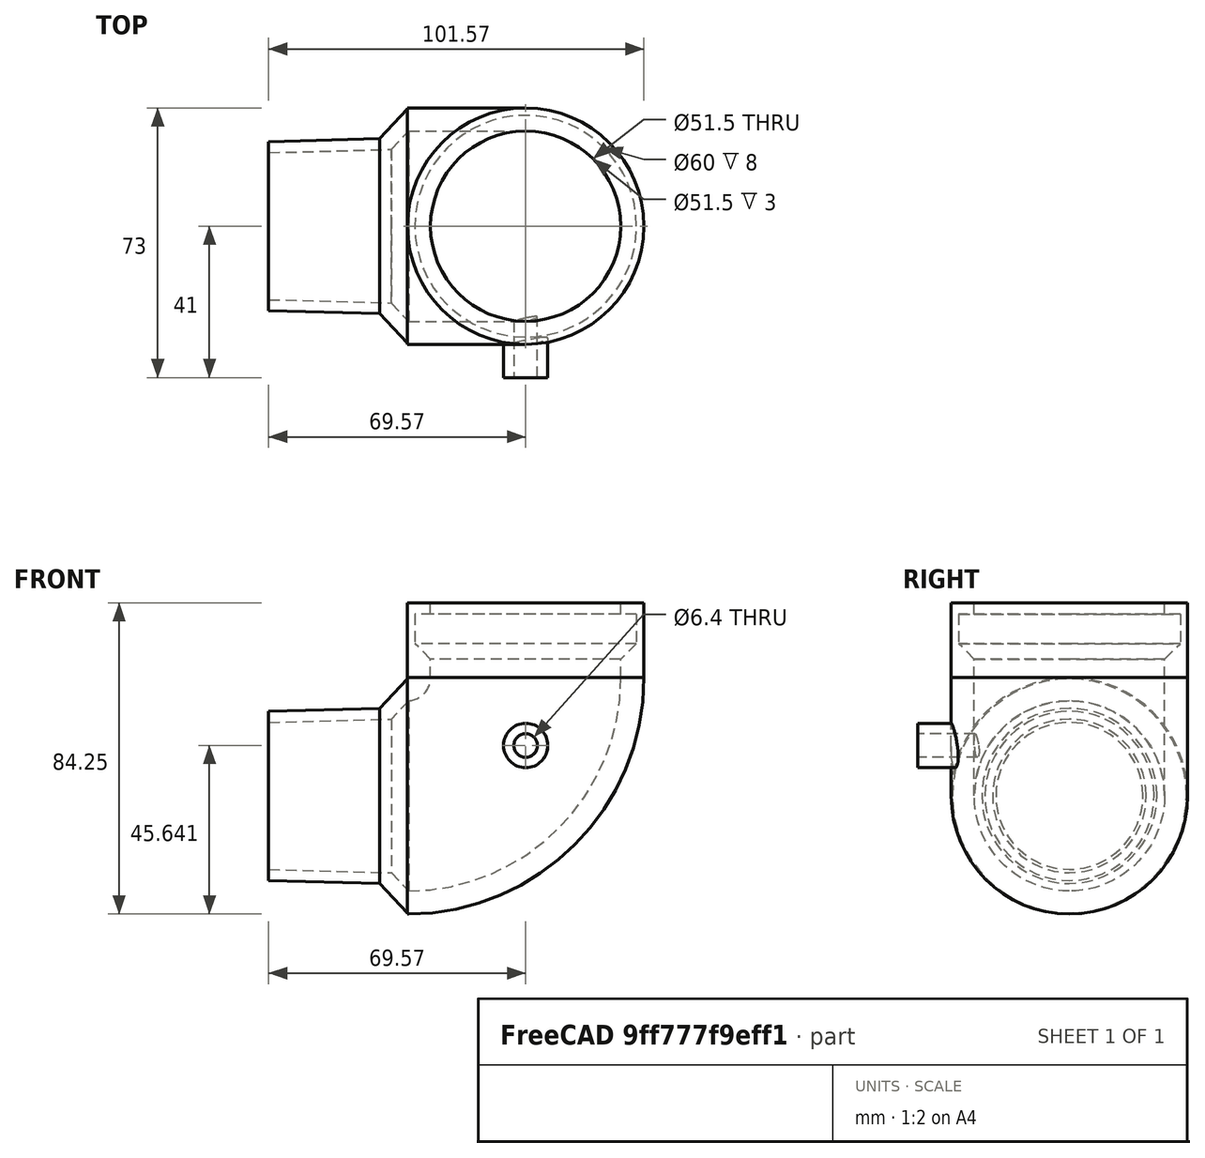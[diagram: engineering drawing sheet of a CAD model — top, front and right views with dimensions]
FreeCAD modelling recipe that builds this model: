
FCSTD DOCUMENT  (FreeCAD 1.1R39747 (Git))
Label: горло (7)
License: All rights reserved
LicenseURL: https://en.wikipedia.org/wiki/All_rights_reserved
objects: Sketcher::SketchObject×5, PartDesign::Revolution×2, App::Point×1, PartDesign::AdditivePipe×1, Part::DatumLine×1, PartDesign::Pad×1, PartDesign::Pocket×1, PartDesign::Body×1
note: 26 computed .brp shape members not serialized (recipe doc carries the construction recipe); baked Part::Feature solids carry a one-line shape summary decoded from their .brp

FEATURE [App::Point] Origin001
  Role = Origin
FEATURE [Sketcher::SketchObject] Sketch
  ArcFitTolerance = 1e-06
  AttachmentSupport = -> [XZ_Plane]
  ExternalTypes = [0]
  FullyConstrained = true
  MakeInternals = false
  MapMode = 5
  Placement = pos=(0,0,0) rot=(1,0,0;1.5708rad)
  expr: Constraints[16] = 63 / 2 - 1.8 + 0.3
  expr: Constraints[17] = 50 / 2 + 0.75
  sketch-geometry (8):
    g0: LineSegment StartX=25.75 StartY=0 StartZ=0 EndX=25.75 EndY=5 EndZ=0
    g1: LineSegment StartX=30 StartY=17.25 StartZ=0 EndX=30 EndY=9.25 EndZ=0
    g2: LineSegment StartX=30 StartY=9.25 StartZ=0 EndX=25.75 EndY=5 EndZ=0
    g3: LineSegment StartX=30 StartY=17.25 StartZ=0 EndX=25.75 EndY=17.25 EndZ=0
    g4: LineSegment StartX=25.75 StartY=17.25 StartZ=0 EndX=25.75 EndY=20.25 EndZ=0
    g5: LineSegment StartX=25.75 StartY=20.25 StartZ=0 EndX=32 EndY=20.25 EndZ=0
    g6: LineSegment StartX=32 StartY=20.25 StartZ=0 EndX=32 EndY=0 EndZ=0
    g7: LineSegment StartX=25.75 StartY=0 StartZ=0 EndX=32 EndY=0 EndZ=0
  constraints (25):
    c: Vertical(g0)
    c: Vertical(g1)
    c: Coincident(g2,g0)
    c: Coincident(g1,g2)
    c: Distance(g1,g1) = 8
    c: Coincident(g3,g1)
    c: Horizontal(g3)
    c: Coincident(g4,g3)
    c: Vertical(g4)
    c: Coincident(g5,g4)
    c: Horizontal(g5)
    c: Coincident(g6,g5)
    c: Vertical(g6)
    c: Distance(g3,g4) = 3  'L1'
    c: DistanceX(g1,g6) = 2
    c: Angle(g0,g2) = 2.35619
    c: DistanceX(g-1,g1) = 30
    c: DistanceX(g-1,g0) = 25.75
    c: Horizontal(g0,g6)
    c: Vertical(g0,g3)
    c: Coincident(g7,g0)
    c: Coincident(g7,g6)
    c: PointOnObject(g0,g-1)
    c: DistanceY(g0,g0) = 5
    c: DistanceX(g-1,g6) = 32  'L2'
FEATURE [PartDesign::Revolution] Revolution
  Angle = 360
  Angle2 = 60
  Axis = (0,2e-16,1)
  Base = (0,0,0)
  Placement = pos=(0,0,0) rot=(1,0,0;1.5708rad)
  Profile = -> Sketch
  ReferenceAxis = -> Sketch [V_Axis]
  Reversed = true
  Suppressed = false
  Type = 0
FEATURE [Sketcher::SketchObject] Sketch002
  ArcFitTolerance = 1e-06
  AttachmentSupport = -> [XZ_Plane]
  ExternalGeometry = -> [Revolution]
  ExternalTypes = [0]
  FullyConstrained = true
  MakeInternals = false
  MapMode = 5
  Placement = pos=(0,0,0) rot=(1,0,0;1.5708rad)
  sketch-geometry (1):
    g0: ArcOfCircle CenterX=-32 CenterY=0 CenterZ=0 NormalX=0 NormalY=0 NormalZ=1 AngleXU=0 Radius=32 StartAngle=4.71239 EndAngle=6.28319
  constraints (3):
    c: Coincident(g0,g-3)
    c: Vertical(g0,g0)
    c: Coincident(g0,g-1)
FEATURE [PartDesign::AdditivePipe] AdditivePipe
  AuxilleryCurvelinear = true
  AuxillerySpineTangent = false
  BaseFeature = -> Revolution
  Binormal = (0,0,0)
  Mode = 0
  Placement = pos=(0,0,0) rot=(1,0,0;1.5708rad)
  Profile = -> Revolution [Face8]
  Refine = true
  Sections = -> [Revolution]
  Spine = -> Sketch002
  SpineTangent = false
  Suppressed = false
  Transformation = 1
  Transition = 1
FEATURE [Sketcher::SketchObject] Sketch003
  ArcFitTolerance = 1e-06
  AttachmentOffset = pos=(0,-3,0) rot=(0,0,1;0rad)
  AttachmentSupport = -> [XZ_Plane]
  ExternalGeometry = -> [AdditivePipe]
  ExternalTypes = [0,0]
  FullyConstrained = false
  MakeInternals = false
  MapMode = 5
  Placement = pos=(0,-7e-16,-3) rot=(1,0,0;1.5708rad)
  expr: Constraints[5] = (50 - 1.8 * 2) / 2 - 0.3
  expr: Constraints[6] = (50 - 1.8 * 2) / 2 + 0.5
  sketch-geometry (7):
    g0: LineSegment StartX=-69.7682 StartY=-6.1 StartZ=0 EndX=-69.7682 EndY=-9.1 EndZ=0
    g1: LineSegment StartX=-69.7682 StartY=-9.1 StartZ=0 EndX=-36.6071 EndY=-8.2157 EndZ=0
    g2: LineSegment StartX=-39.7682 StartY=-5.3 StartZ=0 EndX=-69.7682 EndY=-6.1 EndZ=0
    g3: GeomPoint X=-32 Y=-29 Z=0
    g4: LineSegment StartX=-39.7682 StartY=-5.3 StartZ=0 EndX=-31.8994 EndY=3 EndZ=0
    g5: LineSegment StartX=-31.8994 StartY=3 StartZ=0 EndX=-31.8994 EndY=-3.25 EndZ=0
    g6: LineSegment StartX=-31.8994 StartY=-3.25 StartZ=0 EndX=-36.6071 EndY=-8.2157 EndZ=0
  constraints (18):
    c: Coincident(g0,g1)
    c: Coincident(g2,g0)
    c: Parallel(g1,g2)
    c: Vertical(g0)
    c: Symmetric(g-4,g-4,g3)
    c: DistanceY(g3,g0) = 22.9
    c: DistanceY(g3,g2) = 23.7
    c: Coincident(g6,g1)
    c: Coincident(g2,g4)
    c: Parallel(g6,g4)
    c: DistanceY(g0,g0) = 3
    c: Angle(g4,g2) = 2.35619
    c: Coincident(g6,g5)
    c: Coincident(g5,g4)
    c: Horizontal(g-4,g5)
    c: Horizontal(g-3,g4)
    c: Vertical(g5)
    c: DistanceX(g2,g2) = 30
FEATURE [Part::DatumLine] Line
  AttacherType = Attacher::AttachEngineLine
  AttachmentOffset = pos=(0,0,-54) rot=(0,0,1;0rad)
  AttachmentSupport = -> [AdditivePipe]
  MapMode = 42
  Placement = pos=(-54,-9.8e-15,-32) rot=(0.57735,0.57735,0.57735;2.0944rad)
FEATURE [PartDesign::Revolution] Revolution001
  Angle = 360
  Angle2 = 60
  Axis = (1,0,0)
  Base = (-54,-9.8e-15,-32)
  BaseFeature = -> AdditivePipe
  Placement = pos=(0,0,0) rot=(1,0,0;1.5708rad)
  Profile = -> Sketch003
  ReferenceAxis = -> Line
  Refine = true
  Reversed = true
  Suppressed = false
  Type = 0
FEATURE [Sketcher::SketchObject] Sketch004
  ArcFitTolerance = 1e-06
  AttachmentOffset = pos=(0,0,32) rot=(0,0,1;0rad)
  AttachmentSupport = -> [XZ_Plane]
  ExternalTypes = [0,0]
  FullyConstrained = false
  MakeInternals = false
  MapMode = 5
  Placement = pos=(0,-32,7.1e-15) rot=(1,0,0;1.5708rad)
  sketch-geometry (1):
    g0: Circle CenterX=0 CenterY=-18.359 CenterZ=0 NormalX=0 NormalY=0 NormalZ=1 AngleXU=0 Radius=6
  constraints (2):
    c: PointOnObject(g0,g-2)
    c: Diameter(g0) = 12
FEATURE [PartDesign::Pad] Pad
  BaseFeature = -> Revolution001
  Direction = (0,-1,2e-16)
  Length = 9
  Length2 = 3
  Placement = pos=(0,0,0) rot=(1,0,0;1.5708rad)
  Profile = -> Sketch004
  ReferenceAxis = -> Sketch004 [N_Axis]
  Refine = true
  Suppressed = false
  Type = 4
FEATURE [Sketcher::SketchObject] Sketch005
  ArcFitTolerance = 1e-06
  AttachmentSupport = -> [Pad]
  ExternalGeometry = -> [Pad]
  ExternalTypes = [0]
  FullyConstrained = true
  MakeInternals = false
  MapMode = 5
  Placement = pos=(-1.62e-14,-41,2.8e-14) rot=(1,0,0;1.5708rad)
  sketch-geometry (1):
    g0: Circle CenterX=0 CenterY=-18.359 CenterZ=0 NormalX=0 NormalY=0 NormalZ=1 AngleXU=0 Radius=3.2
  constraints (2):
    c: Coincident(g0,g-3)
    c: Diameter(g0) = 6.4
FEATURE [PartDesign::Pocket] Pocket
  BaseFeature = -> Pad
  Direction = (0,1,0)
  Length = 5
  Length2 = 5
  Offset = 2
  Placement = pos=(0,0,0) rot=(1,0,0;1.5708rad)
  Profile = -> Sketch005
  ReferenceAxis = -> Sketch005 [N_Axis]
  Refine = true
  Suppressed = false
  Type = 2
FEATURE [PartDesign::Body] Body
  AllowCompound = false
  Group = -> [Sketch,Revolution,Sketch002,AdditivePipe,Sketch003,Line,Revolution001,Sketch004,Pad,Sketch005,Pocket]
  Origin = -> Origin
  Tip = -> Pocket
